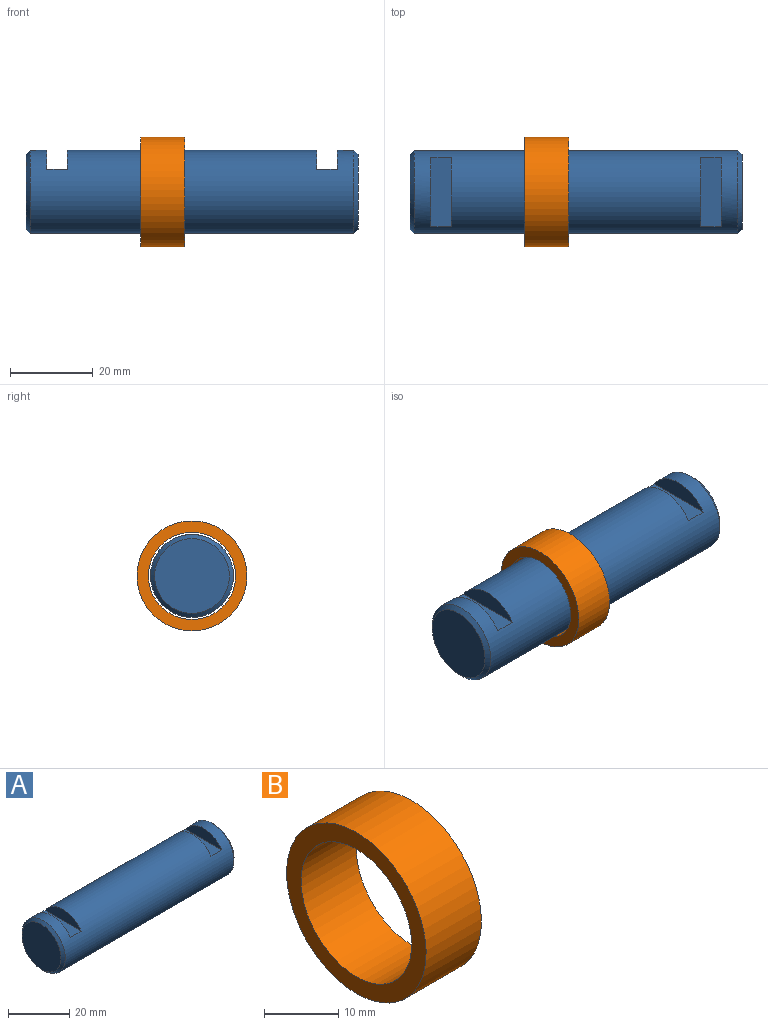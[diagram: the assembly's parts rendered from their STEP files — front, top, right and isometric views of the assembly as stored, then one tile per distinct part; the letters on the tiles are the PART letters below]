
ASSEMBLY  parts=2 mates=1
PART A: 11 faces, bbox 80x20x20 mm
  f0: cylinder r=10mm len=78mm, axis (-1,0,0), area 4703.2mm2, adj f3,f4,f5,f6,f7,f8,f9,f10
  f1: plane 18x18mm, normal (1,0,0), area 254.5mm2, adj f9
  f2: plane 18x18mm, normal (-1,0,0), area 254.5mm2, adj f10
  f3: plane 16.7x4.5mm, normal (1,0,0), area 52.9mm2, adj f0,f5
  f4: plane 16.7x4.5mm, normal (-1,0,0), area 52.9mm2, adj f0,f5
  f5: plane 16.7x5mm, normal (0,0,1), area 83.5mm2, adj f0,f3,f4
  f6: plane 16.7x4.5mm, normal (-1,0,0), area 52.9mm2, adj f0,f8
  f7: plane 16.7x4.5mm, normal (1,0,0), area 52.9mm2, adj f0,f8
  f8: plane 16.7x5mm, normal (0,0,1), area 83.5mm2, adj f0,f6,f7
  f9: cone r=9mm half-angle=45deg, axis (-1,0,0), area 84.4mm2, adj f0,f1
  f10: cone r=10mm half-angle=45deg, axis (1,0,0), area 84.4mm2, adj f0,f2
PART B: 4 faces, bbox 10.5x26.5x26.5 mm
  f0: cylinder r=10.5mm len=21mm, axis (-1,0,0), area 692.7mm2, adj f2,f3
  f1: cylinder r=13.25mm len=26.5mm, axis (-1,0,0), area 874.1mm2, adj f2,f3
  f2: plane 26.5x26.5mm, normal (1,0,0), area 205.2mm2, adj f0,f1
  f3: plane 26.5x26.5mm, normal (-1,0,0), area 205.2mm2, adj f0,f1
PLACE A t=(110.72,60.15,-9.24)mm
PLACE B t=(103.68,247.21,-9.24)mm
MATE slider A.f0 <-> B.f0  axis (-1,0,0) through (110.72,60.15,-9.24)mm
